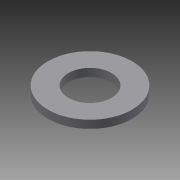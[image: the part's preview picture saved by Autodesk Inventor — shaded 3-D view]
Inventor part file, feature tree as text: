
AUTODESK INVENTOR PART (.ipt)
format: ipt  version: 2013 (Build 170138000, 138)  size: 72,704 bytes
history: native  units: mm
features: extrude x1, sketch x1
ambient origin geometry x8: Origin, YZ Plane, XZ Plane, XY Plane, X Axis, Y Axis, Z Axis, Center Point
bodies: Solid1 (feature_tree)
feature tree (2):
  extrude  "Extrusion1"  Depth=16.0mm
  sketch  "Sketch1"  dims[d0=8.2mm d3=16.0mm d4=1.5mm d5=0.0mm]
